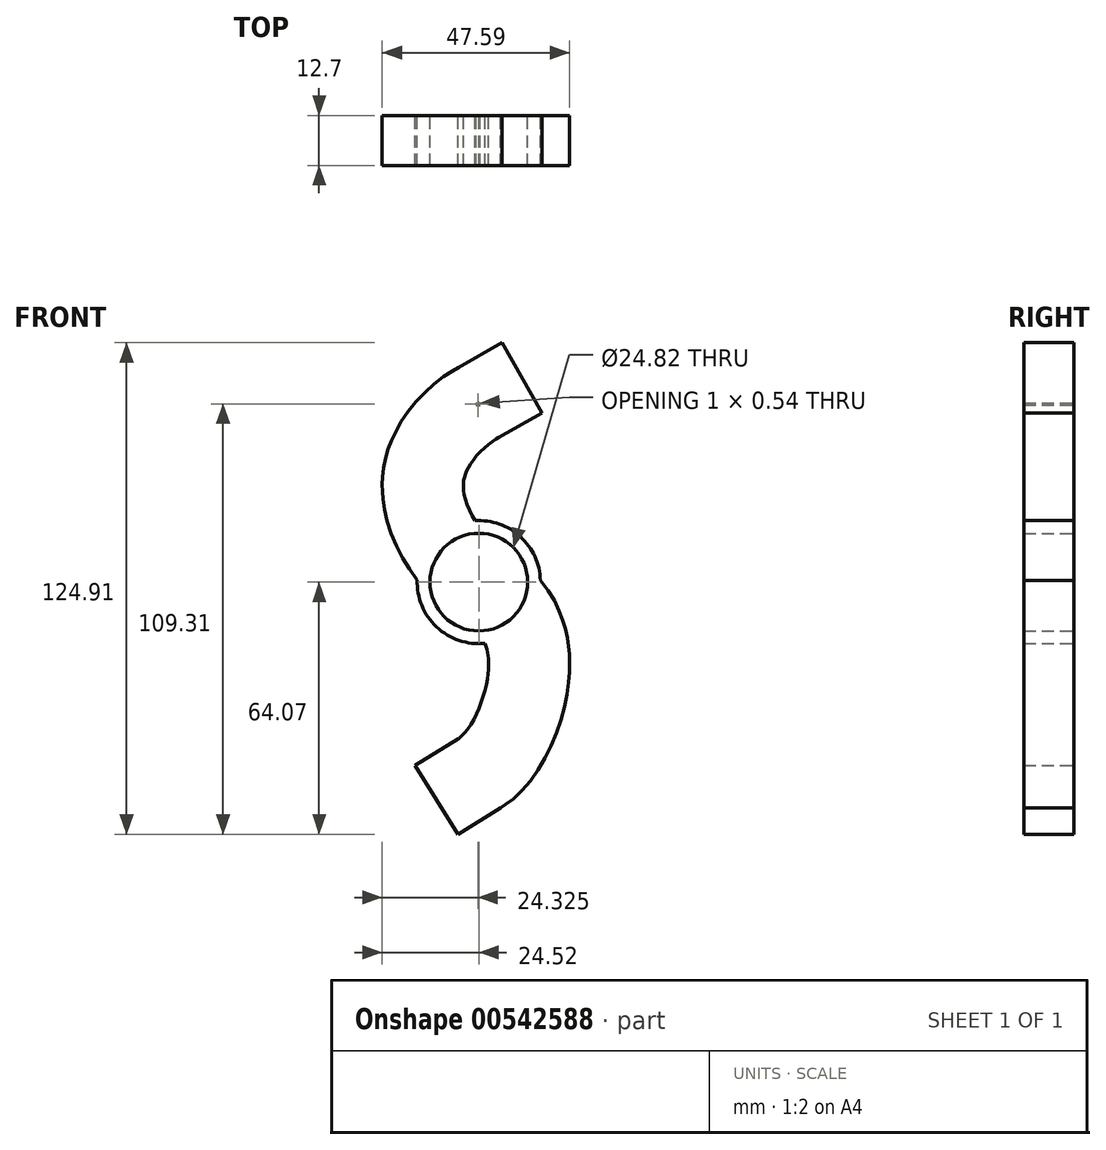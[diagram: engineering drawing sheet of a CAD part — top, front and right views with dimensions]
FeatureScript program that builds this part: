
annotation { "Feature Type Name" : "Feature", "Feature Type Description" : "" }
export const myFeature = defineFeature(function(context is Context, id is Id, definition is map)
    precondition{}
    {
        {
            var Q0;
            Q0=qCreatedBy(makeId("Front.planeOp"),FACE);
            var sketch = newSketch(context, id + "F0", { "sketchPlane" : qUnion([Q0])});
            skFitSpline(sketch, "E0", {"points": [v(0, 0) * mm, v(-14.06, 25.6) * mm, v(0, 45.5) * mm], "startDerivative": vector(-39.9, 24.7) * mm, "endDerivative": vector(38.55, 21.92) * mm});
            skFitSpline(sketch, "E1", {"points": [v(0, 0) * mm, v(12.47, -17.65) * mm, v(0, -48.54) * mm], "startDerivative": vector(41.93, -25.96) * mm, "endDerivative": vector(-43.8, -27.04) * mm});
            skFitSpline(sketch, "E2.0", {"points": [v(5.35, 8.64) * mm, v(5, 8.85) * mm, v(4.09, 9.5) * mm, v(2.43, 11.08) * mm, v(0.72, 13.1) * mm, v(-0.87, 15.42) * mm, v(-2.21, 17.9) * mm, v(-3.21, 20.37) * mm, v(-3.7, 22.27) * mm, v(-3.87, 23.43) * mm, v(-3.92, 24.04) * mm, v(-3.94, 24.46) * mm, v(-3.93, 24.85) * mm, v(-3.9, 25.33) * mm, v(-3.82, 25.95) * mm, v(-3.64, 26.72) * mm, v(-3.37, 27.53) * mm, v(-3.01, 28.37) * mm, v(-2.41, 29.53) * mm, v(-1.44, 31.02) * mm, v(0.04, 32.76) * mm, v(1.7, 34.35) * mm, v(3.44, 35.7) * mm, v(4.53, 36.4) * mm, v(5.02, 36.68) * mm]});
            skFitSpline(sketch, "E3.0", {"points": [v(-5.35, -8.64) * mm, v(-4.67, -9.06) * mm, v(-3.38, -9.92) * mm, v(-1.73, -11.24) * mm, v(-0.4, -12.56) * mm, v(0.65, -13.88) * mm, v(1.3, -15) * mm, v(1.71, -15.96) * mm, v(1.98, -16.73) * mm, v(2.2, -17.56) * mm, v(2.33, -18.33) * mm, v(2.4, -19) * mm, v(2.46, -19.72) * mm, v(2.48, -20.73) * mm, v(2.43, -22.08) * mm, v(2.24, -24) * mm, v(1.79, -26.6) * mm, v(0.9, -29.76) * mm, v(-0.25, -32.8) * mm, v(-1.62, -35.52) * mm, v(-3.08, -37.74) * mm, v(-4.22, -39.01) * mm, v(-4.95, -39.64) * mm, v(-5.23, -39.83) * mm, v(-5.34, -39.9) * mm]});
            skFitSpline(sketch, "E4.0", {"points": [v(5.48, 8.85) * mm, v(6.55, 8.2) * mm, v(8.7, 6.77) * mm, v(11.87, 4.25) * mm, v(14.9, 1.28) * mm, v(17.67, -2.2) * mm, v(19.63, -5.56) * mm, v(20.92, -8.51) * mm, v(21.71, -10.84) * mm, v(22.33, -13.26) * mm, v(22.7, -15.36) * mm, v(22.9, -17.08) * mm, v(23.02, -18.8) * mm, v(23.07, -20.94) * mm, v(22.96, -23.5) * mm, v(22.63, -26.92) * mm, v(21.88, -31.17) * mm, v(20.49, -36.18) * mm, v(18.63, -41.06) * mm, v(16.3, -45.72) * mm, v(13.45, -50.1) * mm, v(10.56, -53.42) * mm, v(7.82, -55.82) * mm, v(6.28, -56.9) * mm, v(5.47, -57.4) * mm]});
            skFitSpline(sketch, "E5.0", {"points": [v(-5.48, -8.85) * mm, v(-6.8, -8.03) * mm, v(-9.28, -6.2) * mm, v(-12.64, -2.99) * mm, v(-15.7, 0.65) * mm, v(-18.44, 4.66) * mm, v(-20.82, 9.03) * mm, v(-22.74, 13.73) * mm, v(-23.87, 17.93) * mm, v(-24.32, 21.01) * mm, v(-24.47, 22.82) * mm, v(-24.52, 24.19) * mm, v(-24.5, 25.58) * mm, v(-24.39, 27.46) * mm, v(-24.07, 29.74) * mm, v(-23.45, 32.35) * mm, v(-22.63, 34.84) * mm, v(-21.63, 37.18) * mm, v(-20.1, 40.11) * mm, v(-17.9, 43.44) * mm, v(-14.93, 46.93) * mm, v(-11.77, 49.94) * mm, v(-8.5, 52.5) * mm, v(-6.27, 53.92) * mm, v(-5.15, 54.56) * mm]});
            skLineSegment(sketch, "E6", {"start": v(-5.34, -39.9) * mm, "end": v(0, -48.54) * mm});
            skLineSegment(sketch, "E7", {"start": v(0, -48.54) * mm, "end": v(5.47, -57.4) * mm});
            skLineSegment(sketch, "E8", {"start": v(-5.15, 54.56) * mm, "end": v(5.02, 36.68) * mm});
            skCircle(sketch, "E9", {"center": v(0, 0) * mm, "radius": 15.65 * mm});
            skLineSegment(sketch, "E10", {"start": v(-5.15, 54.56) * mm, "end": v(0.37, 57.7) * mm});
            skLineSegment(sketch, "E11", {"start": v(5.02, 36.68) * mm, "end": v(16.06, 42.96) * mm});
            skLineSegment(sketch, "E12", {"start": v(9.03, 55.32) * mm, "end": v(16.06, 42.96) * mm});
            skLineSegment(sketch, "E13", {"start": v(-5.34, -39.9) * mm, "end": v(-16.14, -46.57) * mm});
            skLineSegment(sketch, "E14", {"start": v(5.47, -57.4) * mm, "end": v(0.07, -60.74) * mm});
            skLineSegment(sketch, "E15", {"start": v(-16.14, -46.57) * mm, "end": v(-8.67, -58.67) * mm});
            skLineSegment(sketch, "E16", {"start": v(-0.94, 45.13) * mm, "end": v(16.06, 42.96) * mm});
            skLineSegment(sketch, "E17", {"start": v(-5.15, 54.56) * mm, "end": v(10.25, 53.17) * mm});
            skLineSegment(sketch, "E18", {"start": v(-16.14, -46.57) * mm, "end": v(0, -48.54) * mm});
            skLineSegment(sketch, "E19", {"start": v(-10.74, -55.32) * mm, "end": v(5.47, -57.4) * mm});
            skLineSegment(sketch, "E20.0", {"start": v(-14.2, -45.37) * mm, "end": v(-3.4, -62.87) * mm});
            skLineSegment(sketch, "E21.0", {"start": v(3.68, 59.58) * mm, "end": v(13.85, 41.7) * mm});
            skCircle(sketch, "E22", {"center": v(0, 0) * mm, "radius": 12.4 * mm});
            skPoint(sketch, "E23.visualSharp", {"position": v(5.9, 60.84) * mm});
            skPoint(sketch, "E24.visualSharp", {"position": v(-5.34, -64.07) * mm});
            skLineSegment(sketch, "E25", {"start": v(0.37, 57.7) * mm, "end": v(5.9, 60.84) * mm});
            skLineSegment(sketch, "E26", {"start": v(5.9, 60.84) * mm, "end": v(9.03, 55.32) * mm});
            skLineSegment(sketch, "E27", {"start": v(0.07, -60.74) * mm, "end": v(-5.34, -64.07) * mm});
            skLineSegment(sketch, "E28", {"start": v(-5.34, -64.07) * mm, "end": v(-8.67, -58.67) * mm});
            skSolve(sketch);
        }
        {
            var Q0;
            Q0 = qSketchRegion(id + "F0", true);
            extrude(context, id + "F1", {"entities" : qUnion([Q0]), "depth" : 12.7 * mm, "offsetDistance" : 25.4 * mm});
        }
    });
